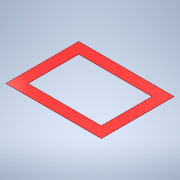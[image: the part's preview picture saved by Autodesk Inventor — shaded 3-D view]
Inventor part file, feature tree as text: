
AUTODESK INVENTOR PART (.ipt)
format: ipt  version: 2022 (Build 260153000, 153)  size: 112,128 bytes
history: native  units: in
note: dims shown in document units (in); Inventor stores cm internally (conversion verified against a paired STEP export)
features: extrude x2, sketch x2
ambient origin geometry x8: Origin, YZ Plane, XZ Plane, XY Plane, X Axis, Y Axis, Z Axis, Center Point
bodies: Solid1 (feature_tree)
feature tree (4):
  extrude  "Extrusion1"  Depth=2.2244in
  extrude  "Extrusion2"  Depth=0.2559in
  sketch  "Sketch1"  dims[d0=1.6969in d1=2.2244in]
  sketch  "Sketch2"  dims[d2=0.0039in d3=0.0in d4=0.2559in d5=0.2559in d6=0.0in d7=0.0in]
